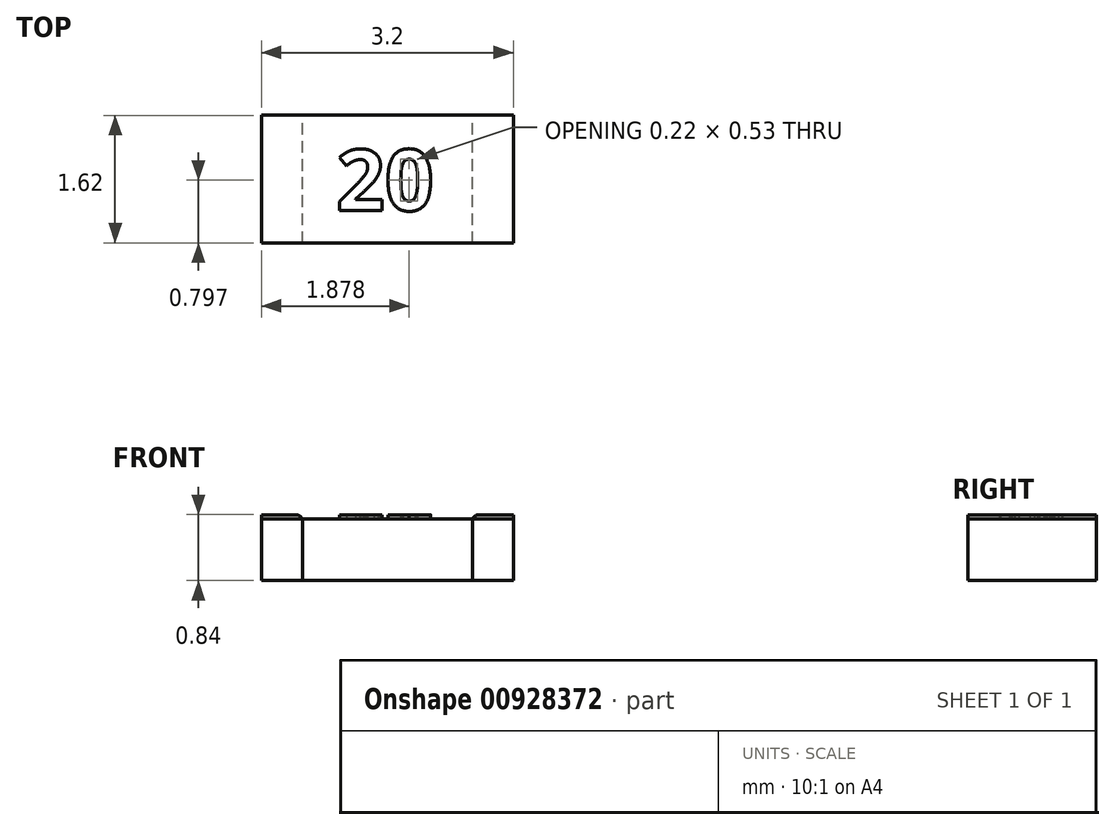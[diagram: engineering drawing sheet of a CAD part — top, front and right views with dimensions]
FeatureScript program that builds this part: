
annotation { "Feature Type Name" : "Feature", "Feature Type Description" : "" }
export const myFeature = defineFeature(function(context is Context, id is Id, definition is map)
    precondition{}
    {
        {
            var Q0;
            Q0=qCreatedBy(makeId("Top.planeOp"),FACE);
            var sketch = newSketch(context, id + "F0", { "sketchPlane" : qUnion([Q0])});
            skLineSegment(sketch, "E0.bottom", {"start": v(-1.6, 0.81) * mm, "end": v(1.6, 0.81) * mm});
            skLineSegment(sketch, "E0.top", {"start": v(-1.6, -0.81) * mm, "end": v(1.6, -0.81) * mm});
            skLineSegment(sketch, "E0.left", {"start": v(-1.6, 0.81) * mm, "end": v(-1.6, -0.81) * mm});
            skLineSegment(sketch, "E0.right", {"start": v(1.6, 0.81) * mm, "end": v(1.6, -0.81) * mm});
            skPoint(sketch, "E0.middle", {"position": v(0, 0) * mm});
            skLineSegment(sketch, "E1", {"start": v(1.6, -0.81) * mm, "end": v(1.08, -0.81) * mm});
            skLineSegment(sketch, "E2", {"start": v(1.08, -0.81) * mm, "end": v(1.08, 0.81) * mm});
            skLineSegment(sketch, "E3", {"start": v(-1.6, -0.81) * mm, "end": v(-1.08, -0.81) * mm});
            skLineSegment(sketch, "E4", {"start": v(-1.08, -0.81) * mm, "end": v(-1.08, 0.81) * mm});
            skSolve(sketch);
        }
        {
            var Q0;
            {var subQ0=sQuery(id+"F0.wireOp",EDGE,"E0.left");Q0=makeQuery(id+"F0.imprint","IMPRINT",FACE,{"disambiguationData":[TD([[makeQuery(id+"F0.imprint","IMPRINT",EDGE,{"derivedFrom":subQ0}),1.0]])]});}
            var Q1;
            {var subQ0=sQuery(id+"F0.wireOp",EDGE,"E0.right");Q1=makeQuery(id+"F0.imprint","IMPRINT",FACE,{"disambiguationData":[TD([[makeQuery(id+"F0.imprint","IMPRINT",EDGE,{"derivedFrom":subQ0}),-1.0]])]});}
            extrude(context, id + "F1", {"entities" : qUnion([Q0, Q1]), "depth" : 0.83 * mm, "offsetDistance" : 25 * mm});
        }
        {
            var Q0;
            Q0=makeQuery(id+"F0.imprint","IMPRINT",FACE,{"disambiguationData":[TD([[makeQuery(id+"F0.imprint","IMPRINT",EDGE,{"derivedFrom":sQuery(id+"F0.wireOp",EDGE,"E0.top")}),1.0]])]});
            extrude(context, id + "F2", {"entities" : qUnion([Q0]), "depth" : 0.79 * mm, "offsetDistance" : 25 * mm});
        }
        {
            var Q0;
            Q0=makeQuery(id+"F2.opExtrude","CAP_FACE",FACE,{"disambiguationData":[OSD([sQuery(id+"F0.wireOp",EDGE,"E0.bottom"),sQuery(id+"F0.wireOp",EDGE,"E0.top"),sQuery(id+"F0.wireOp",EDGE,"E2"),sQuery(id+"F0.wireOp",EDGE,"E4")])],"isStart":false});
            var sketch = newSketch(context, id + "F3", { "sketchPlane" : qUnion([Q0])});
            skText(sketch, "E5", { "text": "20", "fontName": "OpenSans-Bold.ttf"});
            const initialGuessF3  = {"E5": [-0.00065, -0.0004, 1, 0, 0.00078]};
            skSetInitialGuess(sketch, initialGuessF3);
            skSolve(sketch);
        }
        {
            var Q0;
            Q0 = qSketchRegion(id + "F3", true);
            extrude(context, id + "F4", {"entities" : qUnion([Q0]), "depth" : 0.05 * mm, "offsetDistance" : 25 * mm});
        }
        {
            var Q0;
            Q0=makeQuery(id+"F1.opExtrude","CAP_EDGE",EDGE,{"disambiguationData":[OSD([sQuery(id+"F0.wireOp",EDGE,"E2")])],"isStart":false});
            var Q1;
            Q1=makeQuery(id+"F1.opExtrude","CAP_EDGE",EDGE,{"disambiguationData":[OSD([sQuery(id+"F0.wireOp",EDGE,"E4")])],"isStart":false});
            var Q2;
            Q2=makeQuery(id+"F2.opExtrude","CAP_EDGE",EDGE,{"disambiguationData":[OSD([sQuery(id+"F0.wireOp",EDGE,"E4")])],"isStart":true});
            var Q3;
            Q3=makeQuery(id+"F2.opExtrude","CAP_EDGE",EDGE,{"disambiguationData":[OSD([sQuery(id+"F0.wireOp",EDGE,"E2")])],"isStart":true});
            fillet(context, id + "F5", {"entities" : qUnion([Q0, Q1, Q2, Q3]), "radius" : 0.08 * mm, "tangentPropagation" : true, "allowEdgeOverflow" : false});
        }
    });
